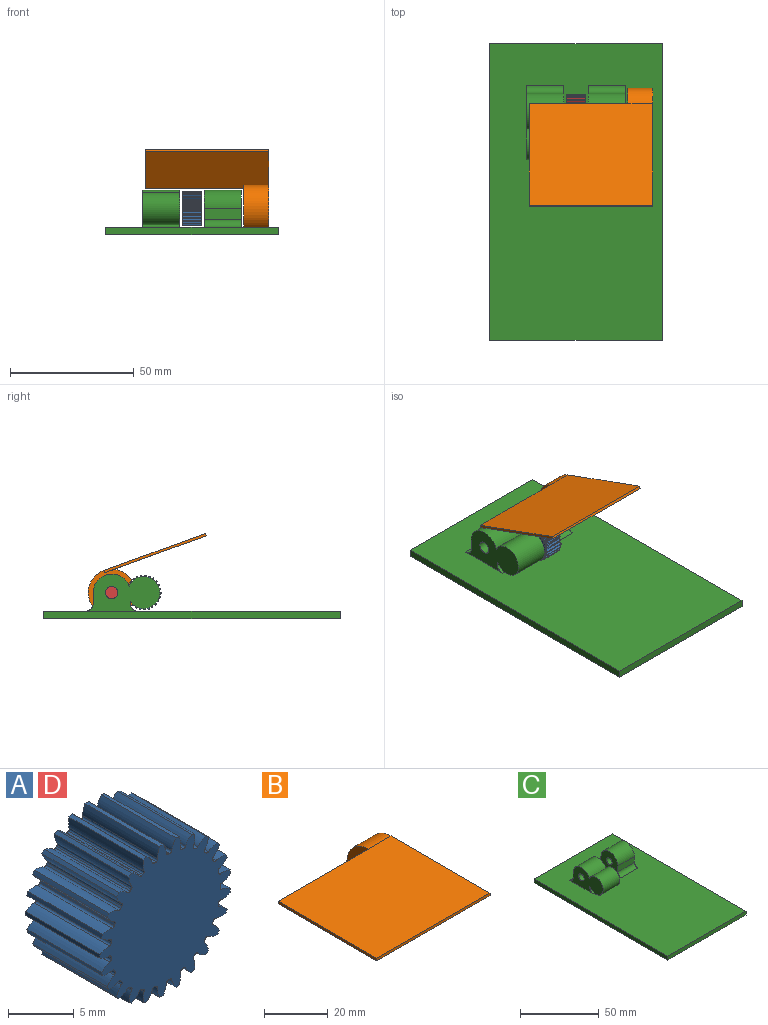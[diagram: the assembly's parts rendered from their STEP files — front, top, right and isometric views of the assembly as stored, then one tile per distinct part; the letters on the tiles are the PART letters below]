
ASSEMBLY  parts=4 mates=3
PART A: 152 faces, bbox 14x8x14 mm
  f0: cylinder r=7.02mm len=8mm, axis (0,1,0), area 3mm2, adj f24,f26,f137,f149
  f1: cylinder r=7.02mm len=8mm, axis (0,1,0), area 3mm2, adj f24,f26,f144,f147
  f2: cylinder r=7.02mm len=8mm, axis (0,1,0), area 3mm2, adj f24,f26,f132,f139
  f3: cylinder r=7.02mm len=8mm, axis (0,1,0), area 3mm2, adj f24,f26,f127,f134
  f4: cylinder r=7.02mm len=8mm, axis (0,1,0), area 3mm2, adj f24,f26,f122,f129
  f5: cylinder r=7.02mm len=8mm, axis (0,1,0), area 3mm2, adj f24,f26,f112,f124
  f6: cylinder r=7.02mm len=8mm, axis (0,1,0), area 3mm2, adj f24,f26,f107,f119
  f7: cylinder r=7.02mm len=8mm, axis (0,1,0), area 3mm2, adj f24,f26,f114,f117
  f8: cylinder r=7.02mm len=8mm, axis (0,1,0), area 3mm2, adj f24,f26,f102,f109
  f9: cylinder r=7.02mm len=8mm, axis (0,1,0), area 3mm2, adj f24,f26,f97,f104
  f10: cylinder r=7.02mm len=8mm, axis (0,1,0), area 3mm2, adj f24,f26,f92,f99
  f11: cylinder r=7.02mm len=8mm, axis (0,1,0), area 3mm2, adj f24,f26,f77,f94
  f12: cylinder r=7.02mm len=8mm, axis (0,1,0), area 3mm2, adj f24,f26,f27,f89
  f13: cylinder r=7.02mm len=8mm, axis (0,1,0), area 3mm2, adj f24,f26,f84,f87
  f14: cylinder r=7.02mm len=8mm, axis (0,1,0), area 3mm2, adj f24,f26,f72,f79
  f15: cylinder r=7.02mm len=8mm, axis (0,1,0), area 3mm2, adj f24,f26,f74,f82
  f16: cylinder r=7.02mm len=8mm, axis (0,1,0), area 3mm2, adj f24,f26,f69,f142
  f17: cylinder r=7.02mm len=8mm, axis (0,1,0), area 3mm2, adj f24,f26,f64,f67
  f18: cylinder r=7.02mm len=8mm, axis (0,1,0), area 3mm2, adj f24,f26,f59,f62
  f19: cylinder r=7.02mm len=8mm, axis (0,1,0), area 3mm2, adj f24,f26,f54,f57
  f20: cylinder r=7.02mm len=8mm, axis (0,1,0), area 3mm2, adj f24,f26,f42,f49
  f21: cylinder r=7.02mm len=8mm, axis (0,1,0), area 3mm2, adj f24,f26,f32,f44
  f22: cylinder r=7.02mm len=8mm, axis (0,1,0), area 3mm2, adj f24,f26,f39,f52
  f23: cylinder r=7.02mm len=8mm, axis (0,1,0), area 3mm2, adj f24,f26,f34,f37
  f24: plane 14.03x14.01mm, normal (0,-1,0), area 130.8mm2, adj f0,f1,f2,f3,f4,f5,f6,f7
  f25: cylinder r=7.02mm len=8mm, axis (0,1,0), area 3mm2, adj f24,f26,f29,f47
  f26: plane 14.03x14.01mm, normal (0,1,0), area 130.8mm2, adj f0,f1,f2,f3,f4,f5,f6,f7
  f27: extruded ~8x0.95mm, area 8.4mm2, adj f12,f24,f26,f30
  f28: cylinder r=5.85mm len=8mm, axis (0,1,0), area 1.4mm2, adj f24,f26,f30,f31
  f29: extruded ~8x0.95mm, area 8.4mm2, adj f24,f25,f26,f31
  f30: cylinder r=0.2mm len=8mm, axis (0,1,0), area 2.4mm2, adj f24,f26,f27,f28
  f31: cylinder r=0.2mm len=8mm, axis (0,1,0), area 2.4mm2, adj f24,f26,f28,f29
  f32: extruded ~8x0.97mm, area 8.4mm2, adj f21,f24,f26,f35
  f33: cylinder r=5.85mm len=8mm, axis (0,1,0), area 1.4mm2, adj f24,f26,f35,f36
  f34: extruded ~8x0.95mm, area 8.4mm2, adj f23,f24,f26,f36
  f35: cylinder r=0.2mm len=8mm, axis (0,1,0), area 2.4mm2, adj f24,f26,f32,f33
  f36: cylinder r=0.2mm len=8mm, axis (0,1,0), area 2.4mm2, adj f24,f26,f33,f34
  f37: extruded ~8x0.85mm, area 8.4mm2, adj f23,f24,f26,f40
  f38: cylinder r=5.85mm len=8mm, axis (0,1,0), area 1.4mm2, adj f24,f26,f40,f41
  f39: extruded ~8x1.02mm, area 8.4mm2, adj f22,f24,f26,f41
  f40: cylinder r=0.2mm len=8mm, axis (0,1,0), area 2.4mm2, adj f24,f26,f37,f38
  f41: cylinder r=0.2mm len=8mm, axis (0,1,0), area 2.4mm2, adj f24,f26,f38,f39
  f42: extruded ~8x1.03mm, area 8.4mm2, adj f20,f24,f26,f45
  f43: cylinder r=5.85mm len=8mm, axis (0,1,0), area 1.4mm2, adj f24,f26,f45,f46
  f44: extruded ~8x0.81mm, area 8.4mm2, adj f21,f24,f26,f46
  f45: cylinder r=0.2mm len=8mm, axis (0,1,0), area 2.4mm2, adj f24,f26,f42,f43
  f46: cylinder r=0.2mm len=8mm, axis (0,1,0), area 2.4mm2, adj f24,f26,f43,f44
  f47: extruded ~8x1.02mm, area 8.4mm2, adj f24,f25,f26,f50
  f48: cylinder r=5.85mm len=8mm, axis (0,1,0), area 1.4mm2, adj f24,f26,f50,f51
  f49: extruded ~8x0.82mm, area 8.4mm2, adj f20,f24,f26,f51
  f50: cylinder r=0.2mm len=8mm, axis (0,1,0), area 2.4mm2, adj f24,f26,f47,f48
  f51: cylinder r=0.2mm len=8mm, axis (0,1,0), area 2.4mm2, adj f24,f26,f48,f49
  f52: extruded ~8x0.78mm, area 8.4mm2, adj f22,f24,f26,f55
  f53: cylinder r=5.85mm len=8mm, axis (0,1,0), area 1.4mm2, adj f24,f26,f55,f56
  f54: extruded ~8x1.03mm, area 8.4mm2, adj f19,f24,f26,f56
  f55: cylinder r=0.2mm len=8mm, axis (0,1,0), area 2.4mm2, adj f24,f26,f52,f53
  f56: cylinder r=0.2mm len=8mm, axis (0,1,0), area 2.4mm2, adj f24,f26,f53,f54
  f57: extruded ~8x0.92mm, area 8.4mm2, adj f19,f24,f26,f60
  f58: cylinder r=5.85mm len=8mm, axis (0,1,0), area 1.4mm2, adj f24,f26,f60,f61
  f59: extruded ~8x0.97mm, area 8.4mm2, adj f18,f24,f26,f61
  f60: cylinder r=0.2mm len=8mm, axis (0,1,0), area 2.4mm2, adj f24,f26,f57,f58
  f61: cylinder r=0.2mm len=8mm, axis (0,1,0), area 2.4mm2, adj f24,f26,f58,f59
  f62: extruded ~8x1.01mm, area 8.4mm2, adj f18,f24,f26,f65
  f63: cylinder r=5.85mm len=8mm, axis (0,1,0), area 1.4mm2, adj f24,f26,f65,f66
  f64: extruded ~8x0.86mm, area 8.4mm2, adj f17,f24,f26,f66
  f65: cylinder r=0.2mm len=8mm, axis (0,1,0), area 2.4mm2, adj f24,f26,f62,f63
  f66: cylinder r=0.2mm len=8mm, axis (0,1,0), area 2.4mm2, adj f24,f26,f63,f64
  f67: extruded ~8x1.03mm, area 8.4mm2, adj f17,f24,f26,f70
  f68: cylinder r=5.85mm len=8mm, axis (0,1,0), area 1.4mm2, adj f24,f26,f70,f71
  f69: extruded ~8x0.77mm, area 8.4mm2, adj f16,f24,f26,f71
  f70: cylinder r=0.2mm len=8mm, axis (0,1,0), area 2.4mm2, adj f24,f26,f67,f68
  f71: cylinder r=0.2mm len=8mm, axis (0,1,0), area 2.4mm2, adj f24,f26,f68,f69
  f72: extruded ~8x0.95mm, area 8.4mm2, adj f14,f24,f26,f75
  f73: cylinder r=5.85mm len=8mm, axis (0,1,0), area 1.4mm2, adj f24,f26,f75,f76
  f74: extruded ~8x0.97mm, area 8.4mm2, adj f15,f24,f26,f76
  f75: cylinder r=0.2mm len=8mm, axis (0,1,0), area 2.4mm2, adj f24,f26,f72,f73
  f76: cylinder r=0.2mm len=8mm, axis (0,1,0), area 2.4mm2, adj f24,f26,f73,f74
  f77: extruded ~8x1.02mm, area 8.4mm2, adj f11,f24,f26,f80
  f78: cylinder r=5.85mm len=8mm, axis (0,1,0), area 1.4mm2, adj f24,f26,f80,f81
  f79: extruded ~8x0.85mm, area 8.4mm2, adj f14,f24,f26,f81
  f80: cylinder r=0.2mm len=8mm, axis (0,1,0), area 2.4mm2, adj f24,f26,f77,f78
  f81: cylinder r=0.2mm len=8mm, axis (0,1,0), area 2.4mm2, adj f24,f26,f78,f79
  f82: extruded ~8x0.81mm, area 8.4mm2, adj f15,f24,f26,f85
  f83: cylinder r=5.85mm len=8mm, axis (0,1,0), area 1.4mm2, adj f24,f26,f85,f86
  f84: extruded ~8x1.03mm, area 8.4mm2, adj f13,f24,f26,f86
  f85: cylinder r=0.2mm len=8mm, axis (0,1,0), area 2.4mm2, adj f24,f26,f82,f83
  f86: cylinder r=0.2mm len=8mm, axis (0,1,0), area 2.4mm2, adj f24,f26,f83,f84
  f87: extruded ~8x0.82mm, area 8.4mm2, adj f13,f24,f26,f90
  f88: cylinder r=5.85mm len=8mm, axis (0,1,0), area 1.4mm2, adj f24,f26,f90,f91
  f89: extruded ~8x1.02mm, area 8.4mm2, adj f12,f24,f26,f91
  f90: cylinder r=0.2mm len=8mm, axis (0,1,0), area 2.4mm2, adj f24,f26,f87,f88
  f91: cylinder r=0.2mm len=8mm, axis (0,1,0), area 2.4mm2, adj f24,f26,f88,f89
  f92: extruded ~8x1.03mm, area 8.4mm2, adj f10,f24,f26,f95
  f93: cylinder r=5.85mm len=8mm, axis (0,1,0), area 1.4mm2, adj f24,f26,f95,f96
  f94: extruded ~8x0.78mm, area 8.4mm2, adj f11,f24,f26,f96
  f95: cylinder r=0.2mm len=8mm, axis (0,1,0), area 2.4mm2, adj f24,f26,f92,f93
  f96: cylinder r=0.2mm len=8mm, axis (0,1,0), area 2.4mm2, adj f24,f26,f93,f94
  f97: extruded ~8x0.97mm, area 8.4mm2, adj f9,f24,f26,f100
  f98: cylinder r=5.85mm len=8mm, axis (0,1,0), area 1.4mm2, adj f24,f26,f100,f101
  f99: extruded ~8x0.92mm, area 8.4mm2, adj f10,f24,f26,f101
  f100: cylinder r=0.2mm len=8mm, axis (0,1,0), area 2.4mm2, adj f24,f26,f97,f98
  f101: cylinder r=0.2mm len=8mm, axis (0,1,0), area 2.4mm2, adj f24,f26,f98,f99
  f102: extruded ~8x0.86mm, area 8.4mm2, adj f8,f24,f26,f105
  f103: cylinder r=5.85mm len=8mm, axis (0,1,0), area 1.4mm2, adj f24,f26,f105,f106
  f104: extruded ~8x1.01mm, area 8.4mm2, adj f9,f24,f26,f106
  f105: cylinder r=0.2mm len=8mm, axis (0,1,0), area 2.4mm2, adj f24,f26,f102,f103
  f106: cylinder r=0.2mm len=8mm, axis (0,1,0), area 2.4mm2, adj f24,f26,f103,f104
  f107: extruded ~8x0.77mm, area 8.4mm2, adj f6,f24,f26,f110
  f108: cylinder r=5.85mm len=8mm, axis (0,1,0), area 1.4mm2, adj f24,f26,f110,f111
  f109: extruded ~8x1.03mm, area 8.4mm2, adj f8,f24,f26,f111
  f110: cylinder r=0.2mm len=8mm, axis (0,1,0), area 2.4mm2, adj f24,f26,f107,f108
  f111: cylinder r=0.2mm len=8mm, axis (0,1,0), area 2.4mm2, adj f24,f26,f108,f109
  f112: extruded ~8x1.01mm, area 8.4mm2, adj f5,f24,f26,f115
  f113: cylinder r=5.85mm len=8mm, axis (0,1,0), area 1.4mm2, adj f24,f26,f115,f116
  f114: extruded ~8x0.89mm, area 8.4mm2, adj f7,f24,f26,f116
  f115: cylinder r=0.2mm len=8mm, axis (0,1,0), area 2.4mm2, adj f24,f26,f112,f113
  f116: cylinder r=0.2mm len=8mm, axis (0,1,0), area 2.4mm2, adj f24,f26,f113,f114
  f117: extruded ~8x0.92mm, area 8.4mm2, adj f7,f24,f26,f120
  f118: cylinder r=5.85mm len=8mm, axis (0,1,0), area 1.4mm2, adj f24,f26,f120,f121
  f119: extruded ~8x0.99mm, area 8.4mm2, adj f6,f24,f26,f121
  f120: cylinder r=0.2mm len=8mm, axis (0,1,0), area 2.4mm2, adj f24,f26,f117,f118
  f121: cylinder r=0.2mm len=8mm, axis (0,1,0), area 2.4mm2, adj f24,f26,f118,f119
  f122: extruded ~8x1.03mm, area 8.4mm2, adj f4,f24,f26,f125
  f123: cylinder r=5.85mm len=8mm, axis (0,1,0), area 1.4mm2, adj f24,f26,f125,f126
  f124: extruded ~8x0.73mm, area 8.4mm2, adj f5,f24,f26,f126
  f125: cylinder r=0.2mm len=8mm, axis (0,1,0), area 2.4mm2, adj f24,f26,f122,f123
  f126: cylinder r=0.2mm len=8mm, axis (0,1,0), area 2.4mm2, adj f24,f26,f123,f124
  f127: extruded ~8x0.99mm, area 8.4mm2, adj f3,f24,f26,f130
  f128: cylinder r=5.85mm len=8mm, axis (0,1,0), area 1.4mm2, adj f24,f26,f130,f131
  f129: extruded ~8x0.89mm, area 8.4mm2, adj f4,f24,f26,f131
  f130: cylinder r=0.2mm len=8mm, axis (0,1,0), area 2.4mm2, adj f24,f26,f127,f128
  f131: cylinder r=0.2mm len=8mm, axis (0,1,0), area 2.4mm2, adj f24,f26,f128,f129
  f132: extruded ~8x0.89mm, area 8.4mm2, adj f2,f24,f26,f135
  f133: cylinder r=5.85mm len=8mm, axis (0,1,0), area 1.4mm2, adj f24,f26,f135,f136
  f134: extruded ~8x0.99mm, area 8.4mm2, adj f3,f24,f26,f136
  f135: cylinder r=0.2mm len=8mm, axis (0,1,0), area 2.4mm2, adj f24,f26,f132,f133
  f136: cylinder r=0.2mm len=8mm, axis (0,1,0), area 2.4mm2, adj f24,f26,f133,f134
  f137: extruded ~8x0.73mm, area 8.4mm2, adj f0,f24,f26,f140
  f138: cylinder r=5.85mm len=8mm, axis (0,1,0), area 1.4mm2, adj f24,f26,f140,f141
  f139: extruded ~8x1.03mm, area 8.4mm2, adj f2,f24,f26,f141
  f140: cylinder r=0.2mm len=8mm, axis (0,1,0), area 2.4mm2, adj f24,f26,f137,f138
  f141: cylinder r=0.2mm len=8mm, axis (0,1,0), area 2.4mm2, adj f24,f26,f138,f139
  f142: extruded ~8x0.99mm, area 8.4mm2, adj f16,f24,f26,f145
  f143: cylinder r=5.85mm len=8mm, axis (0,1,0), area 1.4mm2, adj f24,f26,f145,f146
  f144: extruded ~8x0.92mm, area 8.4mm2, adj f1,f24,f26,f146
  f145: cylinder r=0.2mm len=8mm, axis (0,1,0), area 2.4mm2, adj f24,f26,f142,f143
  f146: cylinder r=0.2mm len=8mm, axis (0,1,0), area 2.4mm2, adj f24,f26,f143,f144
  f147: extruded ~8x0.89mm, area 8.4mm2, adj f1,f24,f26,f150
  f148: cylinder r=5.85mm len=8mm, axis (0,1,0), area 1.4mm2, adj f24,f26,f150,f151
  f149: extruded ~8x1.01mm, area 8.4mm2, adj f0,f24,f26,f151
  f150: cylinder r=0.2mm len=8mm, axis (0,1,0), area 2.4mm2, adj f24,f26,f147,f148
  f151: cylinder r=0.2mm len=8mm, axis (0,1,0), area 2.4mm2, adj f24,f26,f148,f149
PART B: 8 faces, bbox 50x53.3x19 mm
  f0: plane 19x19mm, normal (-1,0,0), area 280.7mm2, adj f1,f2,f6
  f1: plane 50x43.79mm, normal (0,0,-1), area 2147.2mm2, adj f0,f2,f4,f5,f6,f7
  f2: cylinder r=9.5mm len=19mm, axis (-1,0,0), area 552.9mm2, adj f0,f1,f3,f5
  f3: plane 50x43.79mm, normal (0,0,1), area 2189.6mm2, adj f2,f4,f5,f6,f7
  f4: plane 50x1mm, normal (0,-1,0), area 50mm2, adj f1,f3,f5,f7
  f5: plane 53.29x19mm, normal (1,0,0), area 324.5mm2, adj f1,f2,f3,f4
  f6: plane 40x1mm, normal (0,1,0), area 40mm2, adj f0,f1,f3,f7
  f7: plane 43.79x1mm, normal (-1,0,0), area 43.8mm2, adj f1,f3,f4,f6
PART C: 23 faces, bbox 70x120x18 mm
  f0: plane 15x1.04mm, normal (0,-1,0), area 15.5mm2, adj f13,f14,f18,f22
  f1: plane 15x4.5mm, normal (0,1,0), area 67.5mm2, adj f3,f13,f14,f19
  f2: cylinder r=7.5mm len=15mm, axis (-1,0,0), area 353.4mm2, adj f4,f9,f12,f15
  f3: cylinder r=7.5mm len=15mm, axis (-1,0,0), area 313.8mm2, adj f1,f13,f14,f22
  f4: plane 15x4.5mm, normal (0,-1,0), area 67.5mm2, adj f2,f12,f15,f20
  f5: plane 120x70mm, normal (0,0,1), area 7770mm2, adj f6,f8,f10,f11,f12,f13,f14,f15
  f6: plane 70x3mm, normal (0,-1,0), area 210mm2, adj f5,f7,f10,f11
  f7: plane 120x70mm, normal (0,0,-1), area 8400mm2, adj f6,f8,f10,f11
  f8: plane 70x3mm, normal (0,1,0), area 210mm2, adj f5,f7,f10,f11
  f9: plane 15x4.5mm, normal (0,1,0), area 67.5mm2, adj f2,f12,f15,f21
  f10: plane 120x3mm, normal (1,0,0), area 360mm2, adj f5,f6,f7,f8
  f11: plane 120x3mm, normal (-1,0,0), area 360mm2, adj f5,f6,f7,f8
  f12: plane 21x15mm, normal (-1,0,0), area 185.1mm2, adj f2,f4,f5,f9,f17,f20,f21
  f13: plane 30x15mm, normal (1,0,0), area 313.7mm2, adj f0,f1,f3,f5,f16,f18,f19,f22
  f14: plane 30x15mm, normal (-1,0,0), area 313.7mm2, adj f0,f1,f3,f5,f16,f18,f19,f22
  f15: plane 21x15mm, normal (1,0,0), area 185.1mm2, adj f2,f4,f5,f9,f17,f20,f21
  f16: cylinder r=2.5mm len=15mm, axis (-1,0,0), area 235.6mm2, adj f13,f14
  f17: cylinder r=2.5mm len=15mm, axis (-1,0,0), area 235.6mm2, adj f12,f15
  f18: cylinder r=3mm len=15mm, axis (1,0,0), area 70.7mm2, adj f0,f5,f13,f14
  f19: cylinder r=3mm len=15mm, axis (-1,0,0), area 70.7mm2, adj f1,f5,f13,f14
  f20: cylinder r=3mm len=15mm, axis (1,0,0), area 70.7mm2, adj f4,f5,f12,f15
  f21: cylinder r=3mm len=15mm, axis (-1,0,0), area 70.7mm2, adj f5,f9,f12,f15
  f22: cylinder r=6.5mm len=15mm, axis (1,0,0), area 517.8mm2, adj f0,f3,f13,f14
PART D: same geometry as A
PLACE A rot(axis=(-0.5,0.5,0.71),109.2deg) t=(-39,19.5,10.5)mm
PLACE B rot(axis=(-1,0,0),20deg) t=(-14,35.41,18.49)mm
PLACE C t=(-70,-60,3)mm
PLACE D rot(axis=(-0.63,-0.63,-0.44),132.1deg) t=(-31,32.5,10.5)mm
MATE revolute A.f0 <-> C.f22  axis (-1,0,0) through (-39,19.5,10.5)mm
MATE fastened D.f0 <-> B.f2  axis (1,0,0) through (-31,32.5,10.5)mm
MATE revolute D.f0 <-> C.f2  axis (1,0,0) through (-31,32.5,10.5)mm
